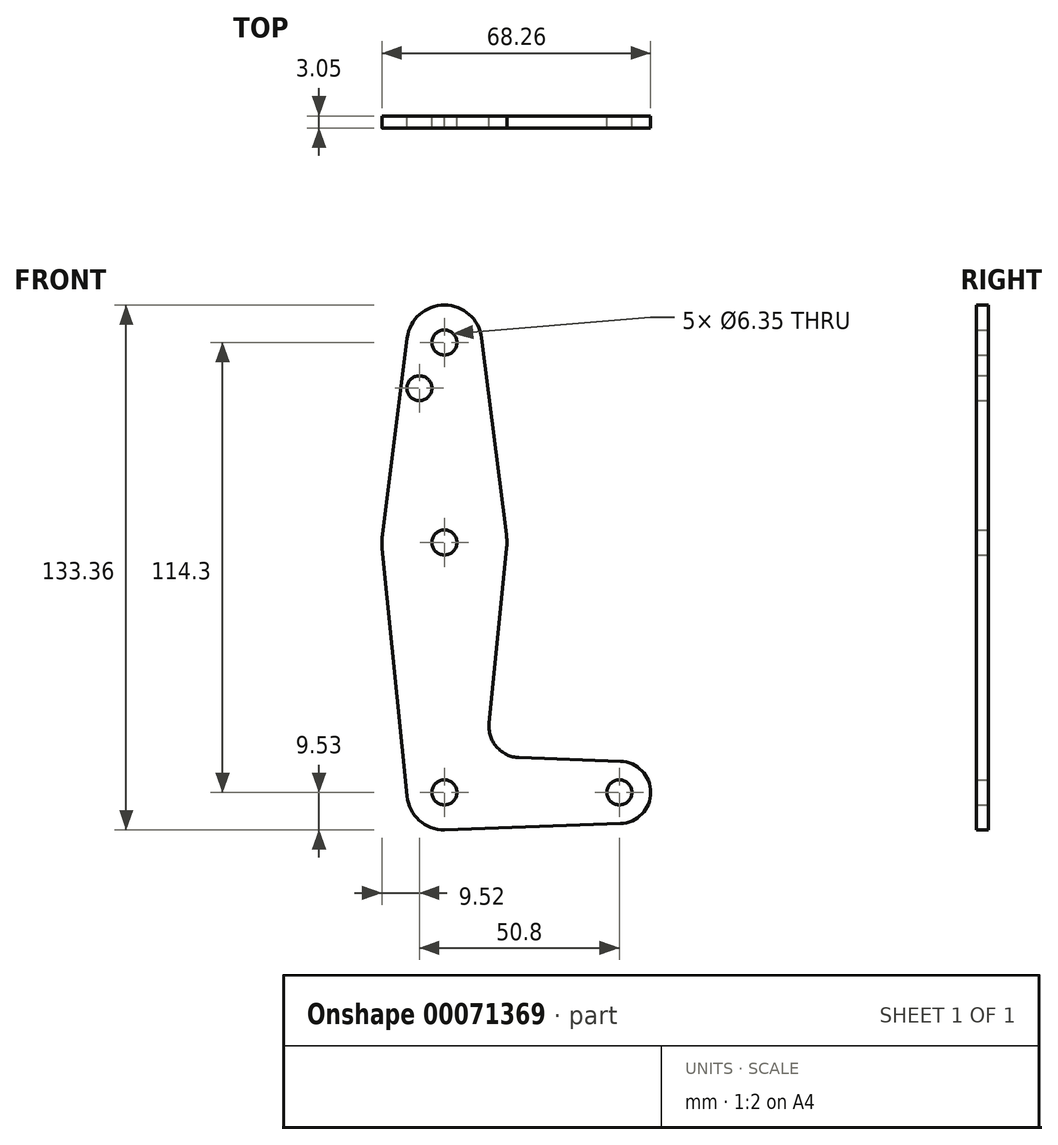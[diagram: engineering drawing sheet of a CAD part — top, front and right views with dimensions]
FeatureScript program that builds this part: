
annotation { "Feature Type Name" : "Feature", "Feature Type Description" : "" }
export const myFeature = defineFeature(function(context is Context, id is Id, definition is map)
    precondition{}
    {
        {
            var Q0;
            Q0=qCreatedBy(makeId("Front.planeOp"),FACE);
            var sketch = newSketch(context, id + "F0", { "sketchPlane" : qUnion([Q0])});
            skLineSegment(sketch, "E0", {"start": v(0, 0) * mm, "end": v(0, 114.3) * mm, "construction": true});
            skLineSegment(sketch, "E1", {"start": v(0, 0) * mm, "end": v(44.45, 0) * mm, "construction": true});
            skCircle(sketch, "E2", {"center": v(0, 0) * mm, "radius": 9.53 * mm});
            skCircle(sketch, "E3", {"center": v(0, 114.3) * mm, "radius": 9.53 * mm});
            skCircle(sketch, "E4", {"center": v(0, 63.5) * mm, "radius": 15.88 * mm});
            skCircle(sketch, "E5", {"center": v(44.45, 0) * mm, "radius": 7.94 * mm});
            skLineSegment(sketch, "E6", {"start": v(-9.45, 115.5) * mm, "end": v(-15.75, 65.48) * mm});
            skLineSegment(sketch, "E7", {"start": v(9.45, 115.5) * mm, "end": v(15.75, 65.48) * mm});
            skLineSegment(sketch, "E8", {"start": v(0, -9.53) * mm, "end": v(44.73, -7.93) * mm});
            skCircle(sketch, "E9", {"center": v(0, 114.3) * mm, "radius": 3.18 * mm});
            skCircle(sketch, "E10", {"center": v(0, 63.5) * mm, "radius": 3.17 * mm});
            skCircle(sketch, "E11", {"center": v(0, 0) * mm, "radius": 3.18 * mm});
            skCircle(sketch, "E12", {"center": v(44.45, 0) * mm, "radius": 3.18 * mm});
            skCircle(sketch, "E13", {"center": v(-6.35, 102.69) * mm, "radius": 3.18 * mm});
            skLineSegment(sketch, "E14", {"start": v(18.97, 8.85) * mm, "end": v(44.73, 7.93) * mm});
            skLineSegment(sketch, "E15", {"start": v(-15.8, 61.91) * mm, "end": v(-9.48, -0.95) * mm});
            skLineSegment(sketch, "E16", {"start": v(15.8, 61.91) * mm, "end": v(11.34, 17.59) * mm});
            skArc(sketch, "E17.filletArc", {"start": v(11.34, 17.59) * mm, "mid": v(13.26, 11.57) * mm, "end": v(18.97, 8.85) * mm});
            skSolve(sketch);
        }
        {
            var Q0;
            {var subQ1=sQuery(id+"F0.wireOp",EDGE,"E6");Q0=makeQuery(id+"F0.imprint","IMPRINT",FACE,{"disambiguationData":[TD([[makeQuery(id+"F0.imprint","IMPRINT",EDGE,{"derivedFrom":subQ1}),1.0]])]});}
            var Q1;
            Q1=makeQuery(id+"F0.imprint","IMPRINT",FACE,{"disambiguationData":[TD([[makeQuery(id+"F0.imprint","IMPRINT",EDGE,{"derivedFrom":sQuery(id+"F0.wireOp",EDGE,"E9")}),-1.0]])]});
            var Q2;
            Q2=makeQuery(id+"F0.imprint","IMPRINT",FACE,{"disambiguationData":[TD([[makeQuery(id+"F0.imprint","IMPRINT",EDGE,{"derivedFrom":sQuery(id+"F0.wireOp",EDGE,"E10")}),-1.0]])]});
            var Q3;
            {var subQ8=sQuery(id+"F0.wireOp",EDGE,"E14");Q3=makeQuery(id+"F0.imprint","IMPRINT",FACE,{"disambiguationData":[TD([[makeQuery(id+"F0.imprint","IMPRINT",EDGE,{"derivedFrom":subQ8}),-1.0]])]});}
            var Q4;
            Q4=makeQuery(id+"F0.imprint","IMPRINT",FACE,{"disambiguationData":[TD([[makeQuery(id+"F0.imprint","IMPRINT",EDGE,{"derivedFrom":sQuery(id+"F0.wireOp",EDGE,"E11")}),-1.0]])]});
            var Q5;
            Q5=makeQuery(id+"F0.imprint","IMPRINT",FACE,{"disambiguationData":[TD([[makeQuery(id+"F0.imprint","IMPRINT",EDGE,{"derivedFrom":sQuery(id+"F0.wireOp",EDGE,"E12")}),-1.0]])]});
            extrude(context, id + "F1", {"entities" : qUnion([Q0, Q1, Q2, Q3, Q4, Q5]), "depth" : 3.05 * mm});
        }
    });
